# Revit family: Centro2.0-Hub
name_source: partatom
category: Lighting Fixtures
revit_build: Autodesk Revit 2018 (Build: 20190510_1515(x64)
units: mm (PartAtom-declared; Revit-internal decimal feet)

## family parameters
Cut with Voids When Loaded = No
Host = Face
Light Source = No
Part Type = Normal
Room Calculation Point = No
Round Connector Dimension = Use Diameter
Shared = Yes

## types (12) — shared parameters
Apparent Load = 0 VA
Code Label Visibility = Yes
Default Elevation = 4' - 0"
Fixture Height = 0' - 4"
Fixture Symbol - Centro - Visibility = Yes
Lamp = LED

## per-type parameters (varying)
| type | 30L - Hub | 45L - Hub | 60L - Hub | 90L - Hub | 90T - Hub | 90X - Hub | Code Label | Manufacturer | Type Comments |
| 135L - Hub | No | No | No | No | No | No | CEN135L |  | LUX ILLUMINAIRE |
| 120L - Hub | No | No | No | No | No | No | CEN120L | LUX ILLUMINAIRE |  |
| 90L - Hub | No | No | No | Yes | No | No | CEN90L | LUX ILLUMINAIRE |  |
| 90T - Hub | No | No | No | No | Yes | No | CEN90T | LUX ILLUMINAIRE |  |
| 90X - Hub | No | No | No | No | No | Yes | CEN90X | LUX ILLUMINAIRE |  |
| 120Y - Hub | No | No | No | No | No | No | CEN120Y | LUX ILLUMINAIRE |  |
| 135Y - Hub | No | No | No | No | No | No | CEN135Y | LUX ILLUMINAIRE |  |
| 30L - Hub | Yes | No | No | No | No | No | CEN30L | LUX ILLUMINAIRE |  |
| 45L - Hub | No | Yes | No | No | No | No | CEN45L | LUX ILLUMINAIRE |  |
| 60L - Hub | No | No | Yes | No | No | No | CEN60L | LUX ILLUMINAIRE |  |
| 120X - Hub | No | No | No | No | No | No | CEN120X | LUX ILLUMINAIRE |  |
| 135X - Hub | No | No | No | No | No | No | CEN135X | LUX ILLUMINAIRE |  |

type visibility flags (boolean, named after types; folded from table):
- 135L - Hub: Yes: 135L - Hub
- 120L - Hub: Yes: 120L - Hub
- 90L - Hub: Yes: (none)
- 90T - Hub: Yes: (none)
- 90X - Hub: Yes: (none)
- 120Y - Hub: Yes: 120Y - Hub
- 135Y - Hub: Yes: 135Y - Hub
- 30L - Hub: Yes: (none)
- 45L - Hub: Yes: (none)
- 60L - Hub: Yes: (none)
- 120X - Hub: Yes: 120X - Hub
- 135X - Hub: Yes: 135X - Hub

## geometry (parser evidence)
native form markers: Sweep x2
no freeform markers — native parametric forms only
